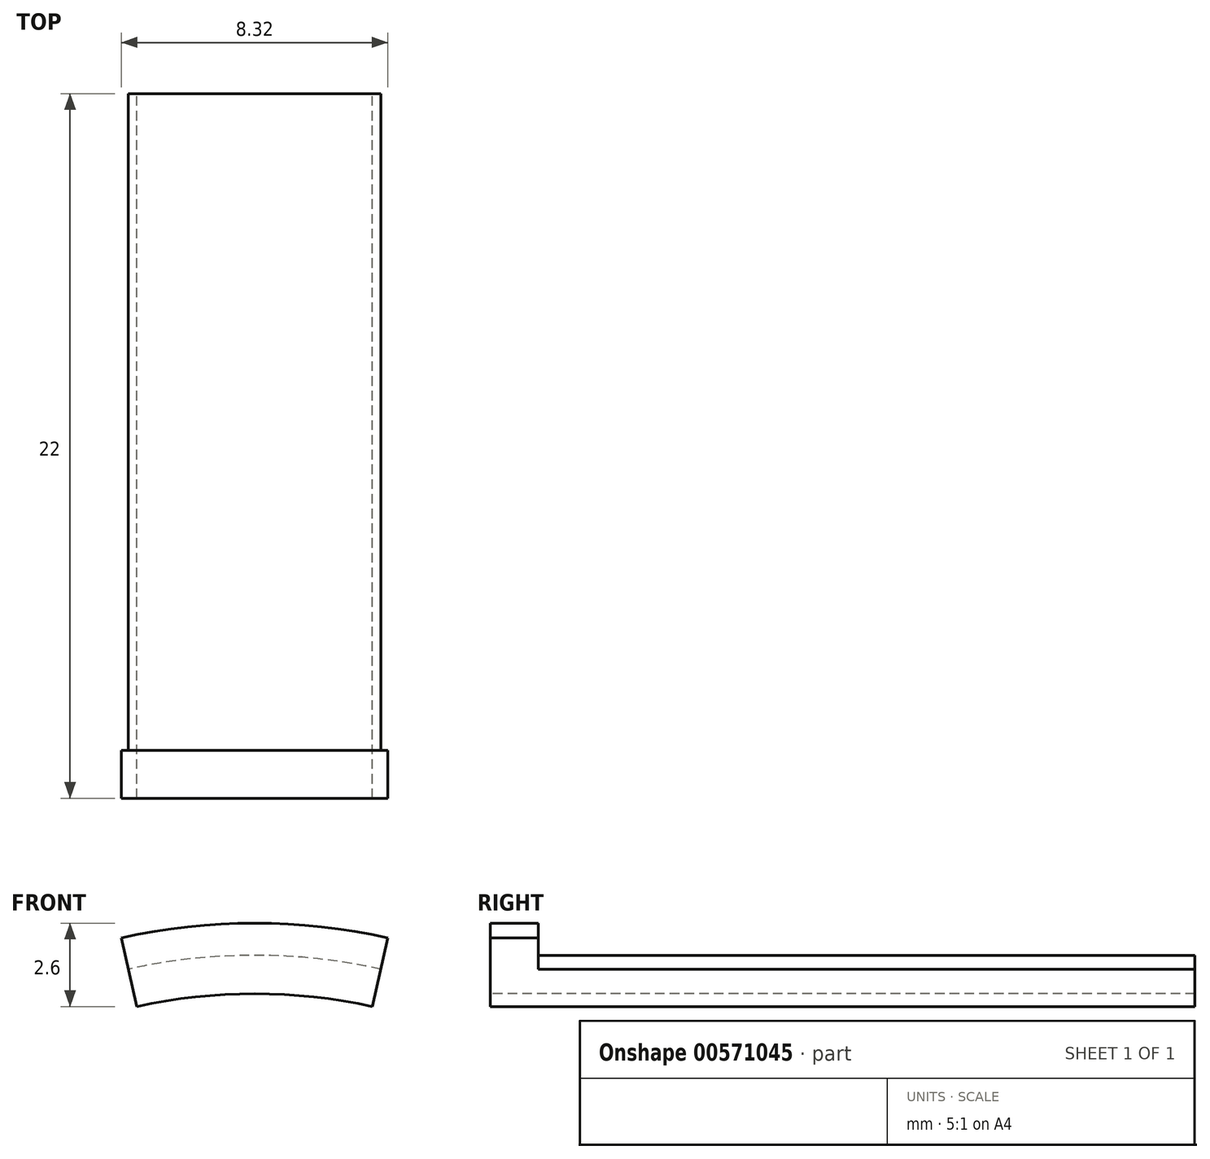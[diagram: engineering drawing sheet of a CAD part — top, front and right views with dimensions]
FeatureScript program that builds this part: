
annotation { "Feature Type Name" : "Feature", "Feature Type Description" : "" }
export const myFeature = defineFeature(function(context is Context, id is Id, definition is map)
    precondition{}
    {
        {
            var Q0;
            Q0=qCreatedBy(makeId("Right.planeOp"),FACE);
            var sketch = newSketch(context, id + "F0", { "sketchPlane" : qUnion([Q0])});
            skLineSegment(sketch, "E0", {"start": v(-16.5, 18.2) * mm, "end": v(-16.5, 19.2) * mm});
            skLineSegment(sketch, "E1", {"start": v(-16.5, 19.2) * mm, "end": v(-18, 19.2) * mm});
            skLineSegment(sketch, "E2", {"start": v(-18, 19.2) * mm, "end": v(-18, 17) * mm});
            skLineSegment(sketch, "E3", {"start": v(-18, 17) * mm, "end": v(0, 17) * mm});
            skLineSegment(sketch, "E4", {"start": v(-108.82, 0) * mm, "end": v(123.32, 0) * mm, "construction": true});
            skLineSegment(sketch, "E5", {"start": v(0, 17) * mm, "end": v(0, 18.2) * mm});
            skLineSegment(sketch, "E6", {"start": v(0, 18.2) * mm, "end": v(-16.5, 18.2) * mm});
            skSolve(sketch);
        }
        {
            var Q0;
            Q0=makeQuery(id+"F0.imprint","IMPRINT",FACE,{"disambiguationData":[TD([[makeQuery(id+"F0.imprint","IMPRINT",EDGE,{"derivedFrom":sQuery(id+"F0.wireOp",EDGE,"E0")}),1.0]])]});
            var Q1;
            Q1=sQuery(id+"F0.wireOp",EDGE,"E4");
            revolve(context, id + "F1", {"entities" : qUnion([Q0]), "axis" : qUnion([Q1]), "revolveType" : RevolveType.TWO_DIRECTIONS, "angle" : 12.5 * degree, "angleBack" : 347.5 * degree});
        }
        {
            var Q0;
            Q0=qCreatedBy(makeId("Right.planeOp"),FACE);
            var sketch = newSketch(context, id + "F2", { "sketchPlane" : qUnion([Q0])});
            skLineSegment(sketch, "E7", {"start": v(0, 17) * mm, "end": v(4, 17) * mm});
            skLineSegment(sketch, "E8", {"start": v(0, 17) * mm, "end": v(0, 18.2) * mm});
            skLineSegment(sketch, "E9", {"start": v(0, 18.2) * mm, "end": v(4, 18.2) * mm});
            skLineSegment(sketch, "E10", {"start": v(4, 18.2) * mm, "end": v(4, 17) * mm});
            skSolve(sketch);
        }
        {
            var Q0;
            Q0 = qSketchRegion(id + "F2", true);
            var Q1;
            Q1=sQuery(id+"F0.wireOp",EDGE,"E4");
            revolve(context, id + "F3", {"operationType" : NewBodyOperationType.ADD, "entities" : qUnion([Q0]), "axis" : qUnion([Q1]), "revolveType" : RevolveType.TWO_DIRECTIONS, "angle" : 12.5 * degree, "angleBack" : 347.5 * degree});
        }
    });
